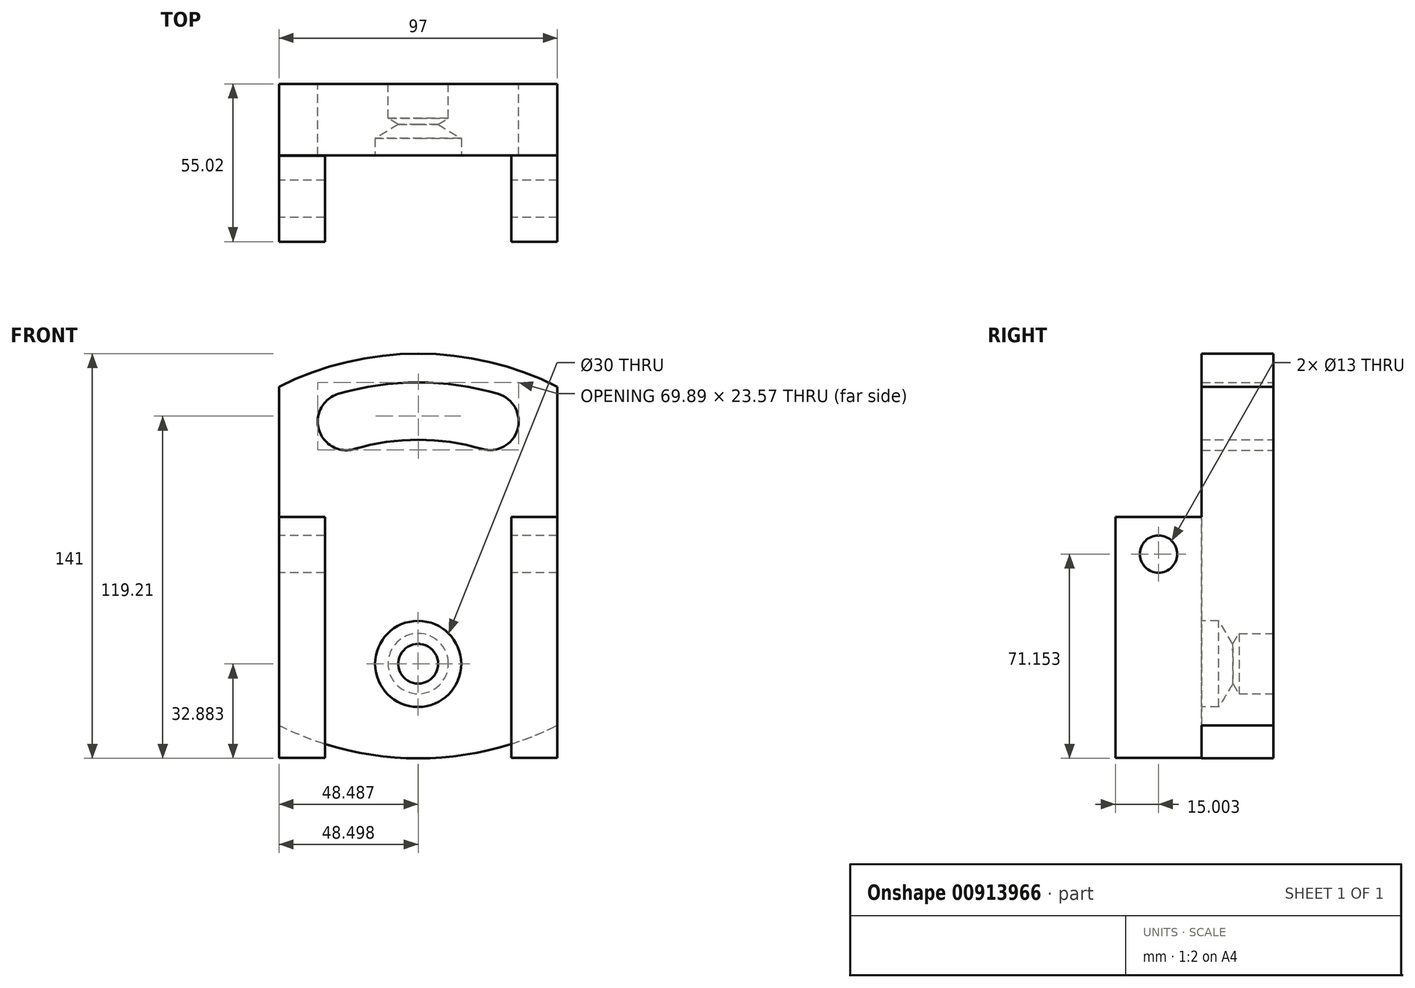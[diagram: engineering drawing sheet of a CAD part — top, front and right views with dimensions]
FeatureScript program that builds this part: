
annotation { "Feature Type Name" : "Feature", "Feature Type Description" : "" }
export const myFeature = defineFeature(function(context is Context, id is Id, definition is map)
    precondition{}
    {
        {
            var Q0;
            Q0=qCreatedBy(makeId("Front.planeOp"),FACE);
            var sketch = newSketch(context, id + "F0", { "sketchPlane" : qUnion([Q0])});
            skLineSegment(sketch, "E0.left", {"start": v(-183.22, 206.33) * mm, "end": v(-183.22, 88.34) * mm});
            skLineSegment(sketch, "E0.right", {"start": v(-86.22, 206.33) * mm, "end": v(-86.22, 88.34) * mm});
            skLineSegment(sketch, "E1", {"start": v(-183.22, 147.34) * mm, "end": v(-86.22, 147.34) * mm, "construction": true});
            skArc(sketch, "E2", {"start": v(-183.22, 88.34) * mm, "mid": v(-134.72, 76.84) * mm, "end": v(-86.22, 88.34) * mm});
            skPoint(sketch, "E3.orphan", {"position": v(-183.22, 76.84) * mm});
            skPoint(sketch, "E4.orphan", {"position": v(-86.22, 76.84) * mm});
            skArc(sketch, "E5", {"start": v(-86.22, 206.33) * mm, "mid": v(-134.72, 217.84) * mm, "end": v(-183.22, 206.33) * mm});
            skPoint(sketch, "E6.orphan", {"position": v(-183.22, 217.84) * mm});
            skPoint(sketch, "E7.orphan", {"position": v(-86.22, 217.84) * mm});
            skLineSegment(sketch, "E8", {"start": v(-134.72, 76.84) * mm, "end": v(-134.72, 217.84) * mm, "construction": true});
            skArc(sketch, "E9.0", {"start": v(-95.2, 188.46) * mm, "mid": v(-102.34, 191.66) * mm, "end": v(-109.72, 194.21) * mm, "construction": true});
            skArc(sketch, "E10", {"start": v(-159.72, 194.21) * mm, "mid": v(-167.1, 191.66) * mm, "end": v(-174.24, 188.46) * mm, "construction": true});
            skArc(sketch, "E11", {"start": v(-109.72, 194.21) * mm, "mid": v(-134.72, 197.84) * mm, "end": v(-159.72, 194.21) * mm, "construction": true});
            skArc(sketch, "E12.0.startCap", {"start": v(-106.88, 203.8) * mm, "mid": v(-100.14, 191.37) * mm, "end": v(-112.56, 184.62) * mm});
            skArc(sketch, "E12.0.endCap", {"start": v(-156.88, 184.62) * mm, "mid": v(-169.3, 191.37) * mm, "end": v(-162.56, 203.8) * mm});
            skArc(sketch, "E12.0.left", {"start": v(-112.56, 184.62) * mm, "mid": v(-134.72, 187.84) * mm, "end": v(-156.88, 184.62) * mm});
            skArc(sketch, "E12.0.right", {"start": v(-106.88, 203.8) * mm, "mid": v(-134.72, 207.84) * mm, "end": v(-162.56, 203.8) * mm});
            skSolve(sketch);
        }
        {
            var Q0;
            Q0 = qSketchRegion(id + "F0", true);
            extrude(context, id + "F1", {"entities" : qUnion([Q0]), "depth" : 25 * mm, "offsetDistance" : 25 * mm});
        }
        {
            var Q0;
            Q0=sQuery(id+"F0.wireOp",VERTEX,"E5.center");
            var Q1;
            Q1=makeQuery(id+"F1.opExtrude","SWEPT_BODY",BODY,{"disambiguationData":[OSD([sQuery(id+"F0.wireOp",EDGE,"E0.left"),sQuery(id+"F0.wireOp",EDGE,"E0.right"),sQuery(id+"F0.wireOp",EDGE,"E2"),sQuery(id+"F0.wireOp",EDGE,"E5")])]});
            hole(context, id + "F2", {"style" : HoleStyle.SIMPLE, "endStyle" : HoleEndStyle.BLIND, "oppositeDirection" : true, "holeDiameter" : 21 * mm, "majorDiameter" : 5 * mm, "holeDepth" : 12 * mm, "isTappedThrough" : true, "tappedDepth" : 12 * mm, "tapClearance" : 3, "locations" : qUnion([Q0]), "scope" : qUnion([Q1])});
        }
        {
            var Q0;
            Q0=makeQuery(id+"F1.opExtrude","CAP_FACE",FACE,{"disambiguationData":[OSD([sQuery(id+"F0.wireOp",EDGE,"E0.left"),sQuery(id+"F0.wireOp",EDGE,"E0.right"),sQuery(id+"F0.wireOp",EDGE,"E2"),sQuery(id+"F0.wireOp",EDGE,"E5")])],"isStart":false});
            var sketch = newSketch(context, id + "F3", { "sketchPlane" : qUnion([Q0])});
            skCircle(sketch, "E13", {"center": v(-134.73, 109.72) * mm, "radius": 15 * mm});
            skSolve(sketch);
        }
        {
            var Q0;
            Q0=sQuery(id+"F3.wireOp",VERTEX,"E13.center");
            var Q1;
            Q1=makeQuery(id+"F1.opExtrude","SWEPT_BODY",BODY,{"disambiguationData":[OSD([sQuery(id+"F0.wireOp",EDGE,"E0.left"),sQuery(id+"F0.wireOp",EDGE,"E0.right"),sQuery(id+"F0.wireOp",EDGE,"E2"),sQuery(id+"F0.wireOp",EDGE,"E5")])]});
            hole(context, id + "F4", {"style" : HoleStyle.SIMPLE, "endStyle" : HoleEndStyle.BLIND, "holeDiameter" : 30 * mm, "majorDiameter" : 5 * mm, "holeDepth" : 6 * mm, "isTappedThrough" : true, "tappedDepth" : 12 * mm, "tapClearance" : 3, "locations" : qUnion([Q0]), "scope" : qUnion([Q1])});
        }
        {
            var Q0;
            Q0=makeQuery(id+"F1.opExtrude","SWEPT_FACE",FACE,{"disambiguationData":[OSD([sQuery(id+"F0.wireOp",EDGE,"E0.right")])]});
            var sketch = newSketch(context, id + "F5", { "sketchPlane" : qUnion([Q0])});
            skLineSegment(sketch, "E14.bottom", {"start": v(-25, 76.95) * mm, "end": v(-55, 76.95) * mm});
            skLineSegment(sketch, "E14.top", {"start": v(-25, 160.95) * mm, "end": v(-55, 160.95) * mm});
            skLineSegment(sketch, "E14.left", {"start": v(-25, 76.95) * mm, "end": v(-25, 160.95) * mm});
            skLineSegment(sketch, "E14.right", {"start": v(-55, 76.95) * mm, "end": v(-55, 160.95) * mm});
            skSolve(sketch);
        }
        {
            var Q0;
            {var subQ3=sQuery(id+"F5.wireOp",EDGE,"E14.bottom");Q0=makeQuery(id+"F5.imprint","IMPRINT",FACE,{"disambiguationData":[TD([[makeQuery(id+"F5.imprint","IMPRINT",EDGE,{"derivedFrom":subQ3}),-1.0]])]});}
            extrude(context, id + "F6", {"entities" : qUnion([Q0]), "operationType" : NewBodyOperationType.ADD, "oppositeDirection" : true, "depth" : 16 * mm, "offsetDistance" : 25 * mm});
        }
        {
            var Q0;
            Q0=makeQuery(id+"F1.opExtrude","SWEPT_FACE",FACE,{"disambiguationData":[OSD([sQuery(id+"F0.wireOp",EDGE,"E0.left")])]});
            var sketch = newSketch(context, id + "F7", { "sketchPlane" : qUnion([Q0])});
            skLineSegment(sketch, "E15.bottom", {"start": v(25.02, 77) * mm, "end": v(55.02, 77) * mm});
            skLineSegment(sketch, "E15.top", {"start": v(25.02, 161) * mm, "end": v(55.02, 161) * mm});
            skLineSegment(sketch, "E15.left", {"start": v(25.02, 77) * mm, "end": v(25.02, 161) * mm});
            skLineSegment(sketch, "E15.right", {"start": v(55.02, 77) * mm, "end": v(55.02, 161) * mm});
            skSolve(sketch);
        }
        {
            var Q0;
            Q0=makeQuery(id+"F7.imprint","IMPRINT",FACE,{"disambiguationData":[TD([[makeQuery(id+"F7.imprint","IMPRINT",EDGE,{"derivedFrom":sQuery(id+"F7.wireOp",EDGE,"E15.bottom")}),1.0]])]});
            extrude(context, id + "F8", {"entities" : qUnion([Q0]), "oppositeDirection" : true, "depth" : 16 * mm, "offsetDistance" : 25 * mm});
        }
        {
            var Q0;
            Q0=makeQuery(id+"F8.opExtrude","CAP_FACE",FACE,{"disambiguationData":[OSD([sQuery(id+"F7.wireOp",EDGE,"E15.bottom"),sQuery(id+"F7.wireOp",EDGE,"E15.top"),sQuery(id+"F7.wireOp",EDGE,"E15.left"),sQuery(id+"F7.wireOp",EDGE,"E15.right")])],"isStart":true});
            var sketch = newSketch(context, id + "F9", { "sketchPlane" : qUnion([Q0])});
            skCircle(sketch, "E16", {"center": v(40.02, 148) * mm, "radius": 6.5 * mm});
            skSolve(sketch);
        }
        {
            var Q0;
            Q0=sQuery(id+"F9.wireOp",VERTEX,"E16.center");
            var Q1;
            Q1=makeQuery(id+"F1.opExtrude","SWEPT_BODY",BODY,{"disambiguationData":[OSD([sQuery(id+"F0.wireOp",EDGE,"E0.left"),sQuery(id+"F0.wireOp",EDGE,"E0.right"),sQuery(id+"F0.wireOp",EDGE,"E2"),sQuery(id+"F0.wireOp",EDGE,"E5")])]});
            var Q2;
            Q2=makeQuery(id+"F8.opExtrude","SWEPT_BODY",BODY,{"disambiguationData":[OSD([sQuery(id+"F7.wireOp",EDGE,"E15.bottom"),sQuery(id+"F7.wireOp",EDGE,"E15.top"),sQuery(id+"F7.wireOp",EDGE,"E15.left"),sQuery(id+"F7.wireOp",EDGE,"E15.right")])]});
            hole(context, id + "F10", {"style" : HoleStyle.SIMPLE, "endStyle" : HoleEndStyle.THROUGH, "holeDiameter" : 13 * mm, "majorDiameter" : 5 * mm, "isTappedThrough" : true, "tappedDepth" : 12 * mm, "tapClearance" : 3, "locations" : qUnion([Q0]), "scope" : qUnion([Q1, Q2])});
        }
        {
            var Q0;
            Q0=makeQuery(id+"F8.opExtrude","SWEPT_FACE",FACE,{"disambiguationData":[OSD([sQuery(id+"F7.wireOp",EDGE,"E15.right")])]});
            var sketch = newSketch(context, id + "F11", { "sketchPlane" : qUnion([Q0])});
            skSolve(sketch);
        }
    });
